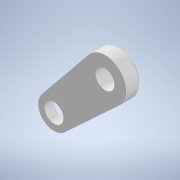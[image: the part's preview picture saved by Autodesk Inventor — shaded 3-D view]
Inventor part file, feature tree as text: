
AUTODESK INVENTOR PART (.ipt)
format: ipt  version: 2022 (Build 260153000, 153)  size: 151,040 bytes
history: native  units: mm
features: other x6, reference x4, sketch x3, extrude x3, fillet x1, chamfer x1, projected_geometry x1
ambient origin geometry x8: Origin, YZ Plane, XZ Plane, XY Plane, X Axis, Y Axis, Z Axis, Center Point
bodies: Body1 (feature_tree)
feature tree (19):
  other  "Твердое тело1"
  sketch  "Эскиз1"
  other  "РабПлоскость1"
  extrude  "Выдавливание1"  Depth=3.6mm
  extrude  "Выдавливание2"  Depth=10.0mm TaperAngle=0.0deg
  fillet  "Сопряжение1"  Radius=3.3mm
  extrude  "Выдавливание3"  Depth=2.0mm TaperAngle=0.0deg
  chamfer  "Фаска1"  Distance=2.0mm
  reference  "Ссылка1"
  sketch  "Эскиз2"
  projected_geometry  "Спроецированная петля1"
  reference  "Ссылка2"
  reference  "Ссылка3"
  sketch  "Эскиз3"
  reference  "Ссылка4"
  other  "<userpath>\Documents\Git\MZCAT_2024\MZCAT_4.iam"
  other  "MZCAT_4.iam"
  other  "OCS-D008 B:3"
  other  "lidar_shatun:1"
